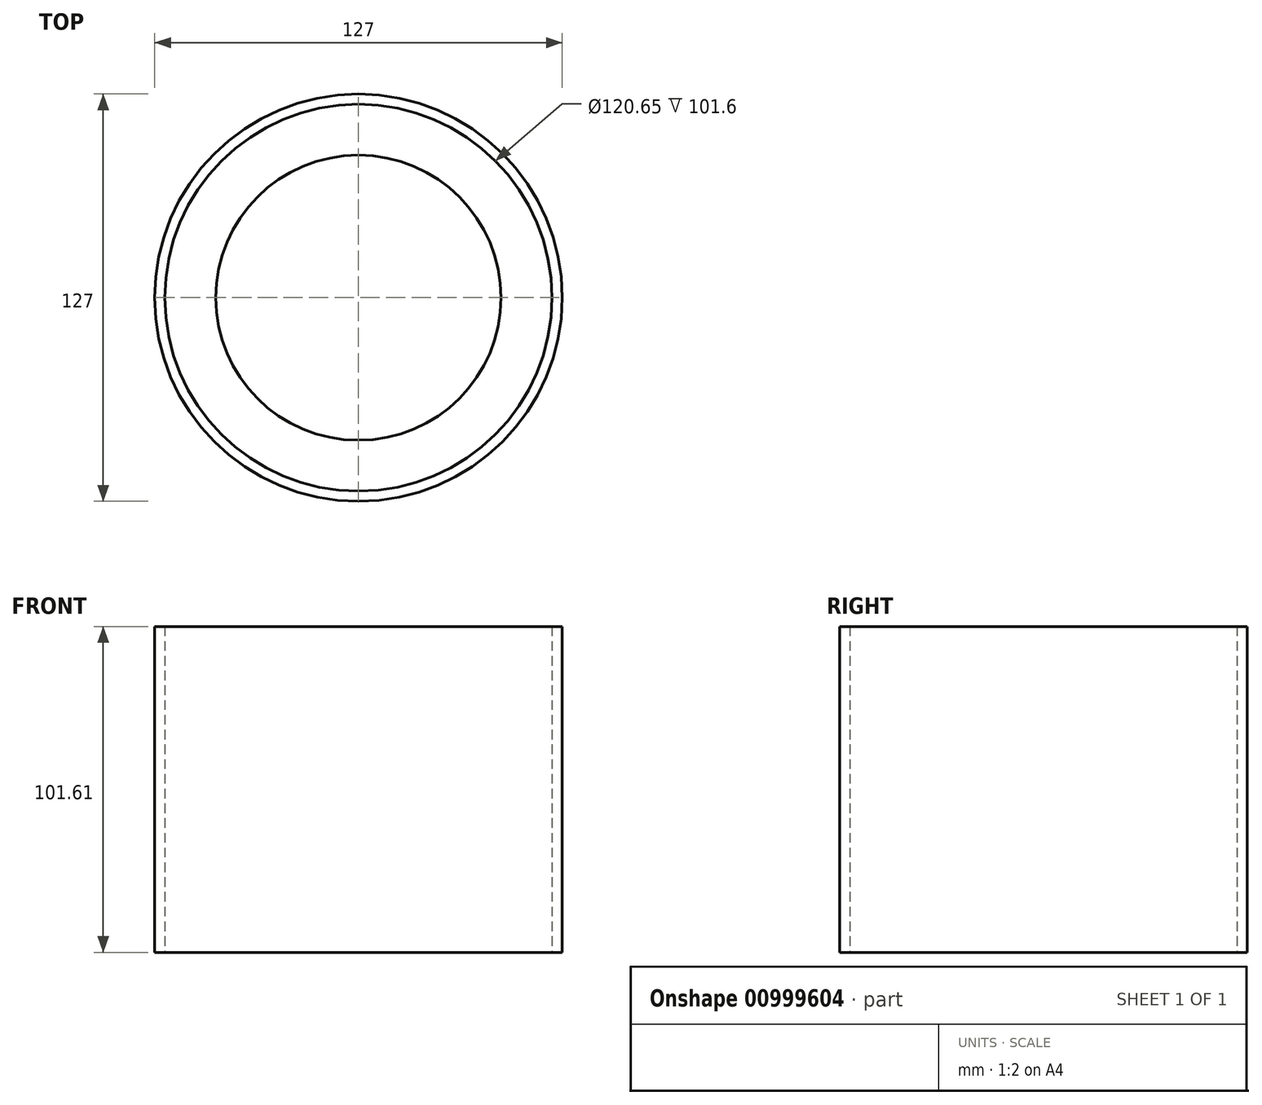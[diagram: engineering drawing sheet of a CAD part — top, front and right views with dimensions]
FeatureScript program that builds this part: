
annotation { "Feature Type Name" : "Feature", "Feature Type Description" : "" }
export const myFeature = defineFeature(function(context is Context, id is Id, definition is map)
    precondition{}
    {
        {
            var Q0;
            Q0=qCreatedBy(makeId("Top.planeOp"),FACE);
            var sketch = newSketch(context, id + "F0", { "sketchPlane" : qUnion([Q0])});
            skCircle(sketch, "E0", {"center": v(0, 0) * mm, "radius": 44.45 * mm});
            skCircle(sketch, "E1", {"center": v(0, 0) * mm, "radius": 63.5 * mm});
            skSolve(sketch);
        }
        {
            var Q0;
            Q0=makeQuery(id+"F0.imprint","IMPRINT",FACE,{"disambiguationData":[TD([[makeQuery(id+"F0.imprint","IMPRINT",EDGE,{"derivedFrom":sQuery(id+"F0.wireOp",EDGE,"E0")}),-1.0]])]});
            extrude(context, id + "F1", {"entities" : qUnion([Q0]), "depth" : 1 / 101.6 * mm, "offsetDistance" : 25.4 * mm});
        }
        {
            var Q0;
            Q0=makeQuery(id+"F1.opExtrude","CAP_FACE",FACE,{"disambiguationData":[OSD([sQuery(id+"F0.wireOp",EDGE,"E0"),sQuery(id+"F0.wireOp",EDGE,"E1")])],"isStart":false});
            var sketch = newSketch(context, id + "F2", { "sketchPlane" : qUnion([Q0])});
            skCircle(sketch, "E2", {"center": v(0, 0) * mm, "radius": 60.33 * mm});
            skCircle(sketch, "E3", {"center": v(0, 0) * mm, "radius": 63.5 * mm});
            skSolve(sketch);
        }
        {
            var Q0;
            Q0=makeQuery(id+"F2.imprint","IMPRINT",FACE,{"disambiguationData":[TD([[makeQuery(id+"F2.imprint","IMPRINT",EDGE,{"derivedFrom":sQuery(id+"F2.wireOp",EDGE,"E2")}),-1.0]])]});
            extrude(context, id + "F3", {"entities" : qUnion([Q0]), "operationType" : NewBodyOperationType.ADD, "depth" : 101.6 * mm, "offsetDistance" : 25.4 * mm});
        }
    });
